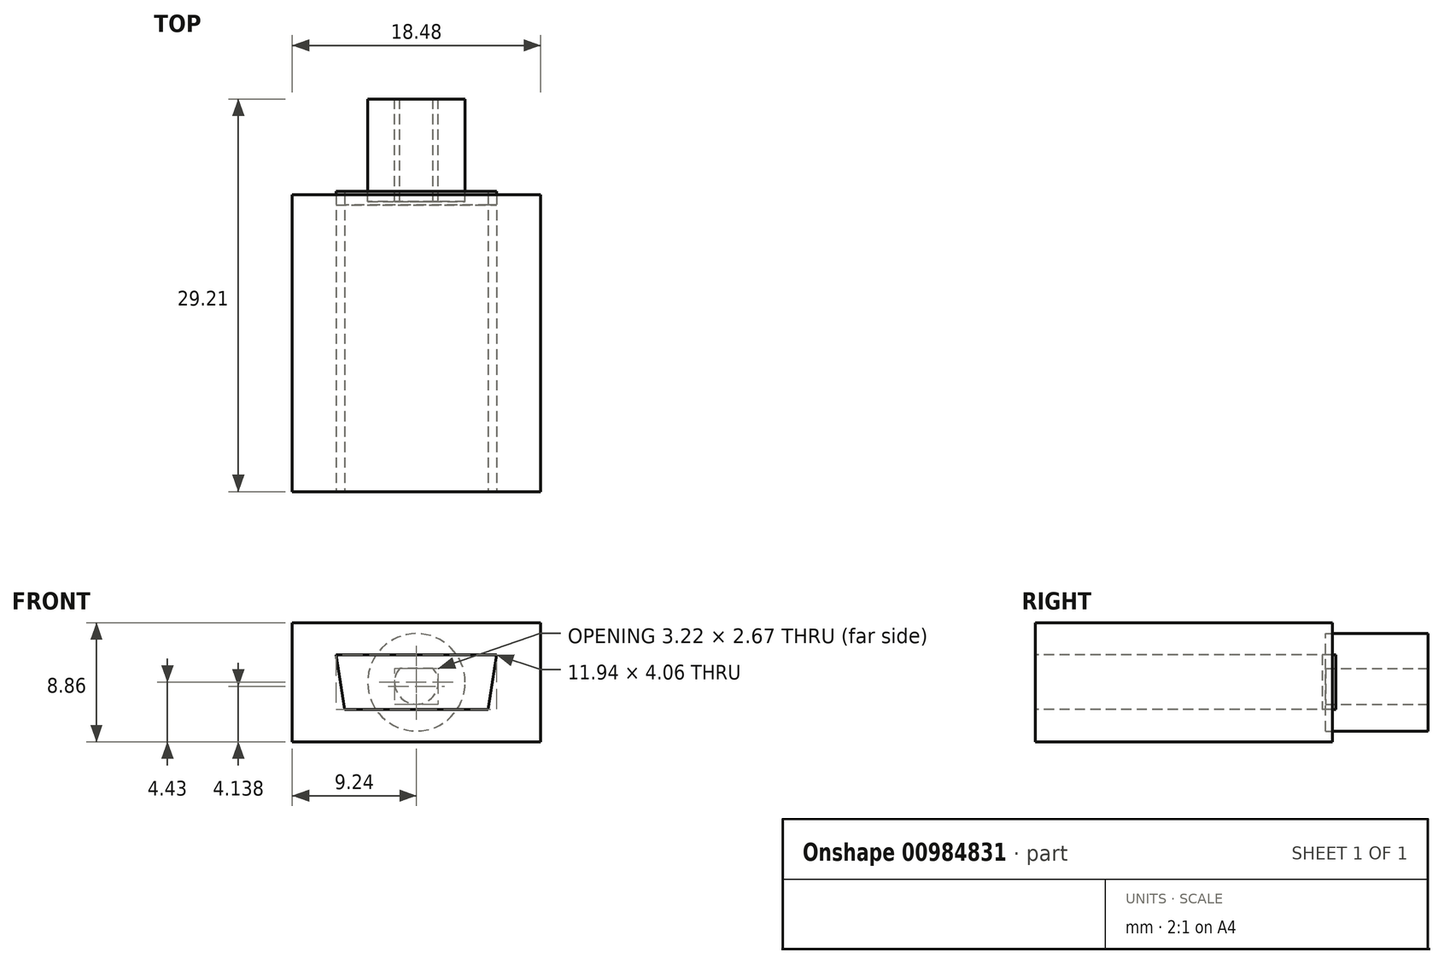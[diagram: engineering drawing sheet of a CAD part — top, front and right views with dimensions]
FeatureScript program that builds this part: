
annotation { "Feature Type Name" : "Feature", "Feature Type Description" : "" }
export const myFeature = defineFeature(function(context is Context, id is Id, definition is map)
    precondition{}
    {
        {
            var Q0;
            Q0=qCreatedBy(makeId("Front.planeOp"),FACE);
            var sketch = newSketch(context, id + "F0", { "sketchPlane" : qUnion([Q0])});
            skArc(sketch, "E0", {"start": v(-1.25, 1.04) * mm, "mid": v(0, -1.63) * mm, "end": v(1.25, 1.04) * mm});
            skLineSegment(sketch, "E1", {"start": v(0.17, 1.04) * mm, "end": v(1.25, 1.04) * mm});
            skLineSegment(sketch, "E2", {"start": v(1.25, 1.04) * mm, "end": v(-1.25, 1.04) * mm});
            skCircle(sketch, "E3", {"center": v(0, 0) * mm, "radius": 3.63 * mm});
            skSolve(sketch);
        }
        {
            var Q0;
            Q0=qCreatedBy(makeId("Front.planeOp"),FACE);
            cPlane(context, id + "F1", {"entities" : qUnion([Q0]), "cplaneType" : CPlaneType.OFFSET, "offset" : 25.4 * mm, "width" : 152.4 * mm, "height" : 152.4 * mm});
        }
        {
            var Q0;
            Q0=qCreatedBy(id+"F1.planeOp",FACE);
            var sketch = newSketch(context, id + "F2", { "sketchPlane" : qUnion([Q0])});
            skPoint(sketch, "E4.start.orphan", {"position": v(-14.68, 3.9) * mm});
            skPoint(sketch, "E5.start.orphan", {"position": v(-44.68, 3.9) * mm});
            skLineSegment(sketch, "E6", {"start": v(0, 2.03) * mm, "end": v(5.97, 2.03) * mm});
            skLineSegment(sketch, "E7", {"start": v(0, -2.03) * mm, "end": v(5.33, -2.03) * mm});
            skLineSegment(sketch, "E8", {"start": v(5.33, -2.03) * mm, "end": v(0, -2.03) * mm});
            skLineSegment(sketch, "E9", {"start": v(0, -2.03) * mm, "end": v(-5.33, -2.03) * mm});
            skLineSegment(sketch, "E10", {"start": v(-5.33, -2.03) * mm, "end": v(0, -2.03) * mm});
            skLineSegment(sketch, "E11", {"start": v(-5.97, 2.03) * mm, "end": v(-5.33, -2.03) * mm});
            skLineSegment(sketch, "E12", {"start": v(5.97, 2.03) * mm, "end": v(5.33, -2.03) * mm});
            skLineSegment(sketch, "E13", {"start": v(-5.97, 2.03) * mm, "end": v(5.97, 2.03) * mm});
            skLineSegment(sketch, "E14", {"start": v(5.33, -2.03) * mm, "end": v(-5.33, -2.03) * mm});
            skPoint(sketch, "E15.start.orphan", {"position": v(0, 0) * mm});
            skLineSegment(sketch, "E16.bottom", {"start": v(9.24, 4.43) * mm, "end": v(-9.24, 4.43) * mm});
            skLineSegment(sketch, "E16.top", {"start": v(9.24, -4.43) * mm, "end": v(-9.24, -4.43) * mm});
            skLineSegment(sketch, "E16.left", {"start": v(9.24, 4.43) * mm, "end": v(9.24, -4.43) * mm});
            skLineSegment(sketch, "E16.right", {"start": v(-9.24, 4.43) * mm, "end": v(-9.24, -4.43) * mm});
            skSolve(sketch);
        }
        {
            var Q0;
            Q0=makeQuery(id+"F0.imprint","IMPRINT",FACE,{"disambiguationData":[TD([[makeQuery(id+"F0.imprint","IMPRINT",EDGE,{"derivedFrom":sQuery(id+"F0.wireOp",EDGE,"E0")}),-1.0]])]});
            extrude(context, id + "F3", {"entities" : qUnion([Q0]), "endBound" : BoundingType.SYMMETRIC, "depth" : 7.62 * mm, "offsetDistance" : 25.4 * mm});
        }
        {
            var Q0;
            Q0 = qSketchRegion(id + "F2", true);
            extrude(context, id + "F4", {"entities" : qUnion([Q0]), "oppositeDirection" : true, "depth" : 22.1 * mm, "offsetDistance" : 25.4 * mm});
        }
        {
            var Q0;
            Q0=makeQuery(id+"F2.imprint","IMPRINT",FACE,{"disambiguationData":[TD([[makeQuery(id+"F2.imprint","IMPRINT",EDGE,{"derivedFrom":sQuery(id+"F2.wireOp",EDGE,"E13")}),-1.0]])]});
            extrude(context, id + "F5", {"entities" : qUnion([Q0]), "oppositeDirection" : true, "depth" : 22.35 * mm, "offsetDistance" : 25.4 * mm});
        }
        {
            var Q0;
            Q0=makeQuery(id+"F5.opExtrude","CAP_FACE",FACE,{"disambiguationData":[OSD([sQuery(id+"F2.wireOp",EDGE,"E13"),sQuery(id+"F2.wireOp",EDGE,"E12"),sQuery(id+"F2.wireOp",EDGE,"E14"),sQuery(id+"F2.wireOp",EDGE,"TwAiB9FC-RQe4-WzCO-q2qG-9pcuuE4Rts4r")])],"isStart":true});
            extrude(context, id + "F6", {"entities" : qUnion([Q0]), "operationType" : NewBodyOperationType.REMOVE, "oppositeDirection" : true, "depth" : 21.34 * mm, "offsetDistance" : 25.4 * mm});
        }
    });
